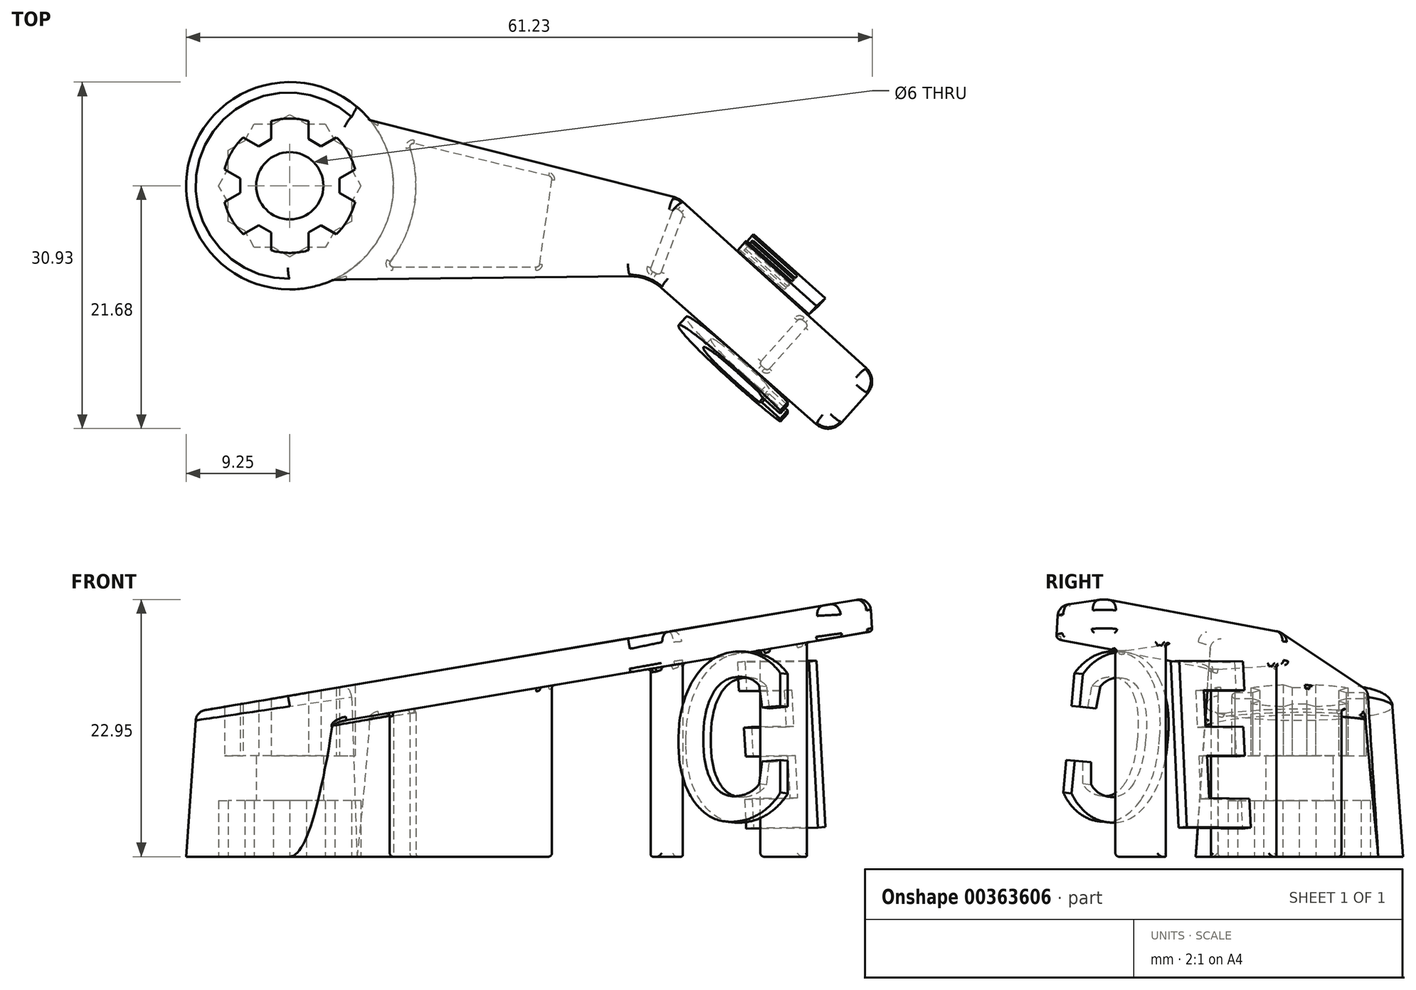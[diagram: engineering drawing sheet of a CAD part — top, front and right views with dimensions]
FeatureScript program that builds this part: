
annotation { "Feature Type Name" : "Feature", "Feature Type Description" : "" }
export const myFeature = defineFeature(function(context is Context, id is Id, definition is map)
    precondition{}
    {
        {
            var Q0;
            Q0=qCreatedBy(makeId("Top.planeOp"),FACE);
            var sketch = newSketch(context, id + "F0", { "sketchPlane" : qUnion([Q0])});
            skCircle(sketch, "E0", {"center": v(0, 0) * mm, "radius": 9.25 * mm});
            skCircle(sketch, "E1", {"center": v(0, 0) * mm, "radius": 3 * mm});
            skLineSegment(sketch, "E2", {"start": v(0, -9.25) * mm, "end": v(30.35, -9.25) * mm});
            skLineSegment(sketch, "E3", {"start": v(32.35, -10.02) * mm, "end": v(46.06, -22.3) * mm});
            skLineSegment(sketch, "E4", {"start": v(50.3, -22.07) * mm, "end": v(52.63, -19.46) * mm});
            skLineSegment(sketch, "E5", {"start": v(52.4, -15.22) * mm, "end": v(35.86, -0.5) * mm});
            skLineSegment(sketch, "E6", {"start": v(34.56, 0.18) * mm, "end": v(6, 7.05) * mm});
            skPoint(sketch, "E7.visualSharp", {"position": v(48.3, -24.3) * mm});
            skArc(sketch, "E7.filletArc", {"start": v(46.06, -22.3) * mm, "mid": v(48.23, -23.06) * mm, "end": v(50.3, -22.07) * mm});
            skPoint(sketch, "E8.visualSharp", {"position": v(54.64, -17.22) * mm});
            skArc(sketch, "E8.filletArc", {"start": v(52.63, -19.46) * mm, "mid": v(53.4, -17.3) * mm, "end": v(52.4, -15.22) * mm});
            skPoint(sketch, "E9.visualSharp", {"position": v(35.3, 0) * mm});
            skArc(sketch, "E9.filletArc", {"start": v(35.86, -0.5) * mm, "mid": v(35.25, -0.08) * mm, "end": v(34.56, 0.18) * mm});
            skPoint(sketch, "E10.visualSharp", {"position": v(31.5, -9.25) * mm});
            skArc(sketch, "E10.filletArc", {"start": v(32.35, -10.02) * mm, "mid": v(31.42, -9.45) * mm, "end": v(30.35, -9.25) * mm});
            skSolve(sketch);
        }
        {
            var Q0;
            Q0=makeQuery(id+"F0.imprint","IMPRINT",FACE,{"disambiguationData":[TD([[makeQuery(id+"F0.imprint","IMPRINT",EDGE,{"derivedFrom":sQuery(id+"F0.wireOp",EDGE,"E1")}),-1.0]])]});
            var Q1;
            Q1=makeQuery(id+"F0.imprint","IMPRINT",FACE,{"disambiguationData":[TD([[makeQuery(id+"F0.imprint","IMPRINT",EDGE,{"derivedFrom":sQuery(id+"F0.wireOp",EDGE,"E1")}),1.0]])]});
            var Q2;
            {var subQ0=sQuery(id+"F0.wireOp",EDGE,"E2");Q2=makeQuery(id+"F0.imprint","IMPRINT",FACE,{"disambiguationData":[TD([[makeQuery(id+"F0.imprint","IMPRINT",EDGE,{"derivedFrom":subQ0}),1.0]])]});}
            extrude(context, id + "F1", {"entities" : qUnion([Q0, Q1, Q2]), "depth" : 23 * mm, "hasDraft" : true, "draftAngle" : 4 * degree, "draftPullDirection" : true});
        }
        {
            var Q0;
            Q0=makeQuery(id+"F0.imprint","IMPRINT",FACE,{"disambiguationData":[TD([[makeQuery(id+"F0.imprint","IMPRINT",EDGE,{"derivedFrom":sQuery(id+"F0.wireOp",EDGE,"E1")}),1.0]])]});
            extrude(context, id + "F2", {"entities" : qUnion([Q0]), "operationType" : NewBodyOperationType.REMOVE, "endBound" : BoundingType.THROUGH_ALL, "depth" : 25 * mm});
        }
        {
            var Q0;
            Q0=makeQuery(id+"F1.opExtrude","CAP_FACE",FACE,{"disambiguationData":[OSD([sQuery(id+"F0.wireOp",EDGE,"E0"),sQuery(id+"F0.wireOp",EDGE,"E2"),sQuery(id+"F0.wireOp",EDGE,"E3"),sQuery(id+"F0.wireOp",EDGE,"E4"),sQuery(id+"F0.wireOp",EDGE,"E5"),sQuery(id+"F0.wireOp",EDGE,"E6"),sQuery(id+"F0.wireOp",EDGE,"E7.filletArc"),sQuery(id+"F0.wireOp",EDGE,"E8.filletArc"),sQuery(id+"F0.wireOp",EDGE,"E9.filletArc"),sQuery(id+"F0.wireOp",EDGE,"E10.filletArc")])],"isStart":false});
            var sketch = newSketch(context, id + "F3", { "sketchPlane" : qUnion([Q0])});
            skCircle(sketch, "E11", {"center": v(0, 0) * mm, "radius": 6 * mm});
            skSolve(sketch);
        }
        {
            var Q0;
            Q0 = qSketchRegion(id + "F3", true);
            extrude(context, id + "F4", {"entities" : qUnion([Q0]), "operationType" : NewBodyOperationType.REMOVE, "oppositeDirection" : true, "depth" : 4.5 * mm});
        }
        {
            var Q0;
            Q0=makeQuery(id+"F0.imprint","IMPRINT",FACE,{"disambiguationData":[TD([[makeQuery(id+"F0.imprint","IMPRINT",EDGE,{"derivedFrom":sQuery(id+"F0.wireOp",EDGE,"E1")}),-1.0]])]});
            var sketch = newSketch(context, id + "F5", { "sketchPlane" : qUnion([Q0])});
            skCircle(sketch, "E12.cCircle", {"center": v(0, 0) * mm, "radius": 5.5 * mm, "construction": true});
            skLineSegment(sketch, "E12.0", {"start": v(5.5, 3.18) * mm, "end": v(5.5, -3.18) * mm});
            skLineSegment(sketch, "E12.1", {"start": v(5.5, -3.18) * mm, "end": v(0, -6.35) * mm});
            skLineSegment(sketch, "E12.2", {"start": v(0, -6.35) * mm, "end": v(-5.5, -3.18) * mm});
            skLineSegment(sketch, "E12.3", {"start": v(-5.5, -3.18) * mm, "end": v(-5.5, 3.18) * mm});
            skLineSegment(sketch, "E12.4", {"start": v(-5.5, 3.18) * mm, "end": v(0, 6.35) * mm});
            skLineSegment(sketch, "E12.5", {"start": v(0, 6.35) * mm, "end": v(5.5, 3.18) * mm});
            skPoint(sketch, "E12.0.midPoint", {"position": v(5.5, 0) * mm});
            skLineSegment(sketch, "E13.0", {"start": v(6.35, 0) * mm, "end": v(3.18, -5.5) * mm});
            skLineSegment(sketch, "E13.1", {"start": v(3.18, -5.5) * mm, "end": v(-3.18, -5.5) * mm});
            skLineSegment(sketch, "E13.2", {"start": v(-3.18, -5.5) * mm, "end": v(-6.35, 0) * mm});
            skLineSegment(sketch, "E13.3", {"start": v(-6.35, 0) * mm, "end": v(-3.18, 5.5) * mm});
            skLineSegment(sketch, "E13.4", {"start": v(-3.18, 5.5) * mm, "end": v(3.18, 5.5) * mm});
            skLineSegment(sketch, "E13.5", {"start": v(3.18, 5.5) * mm, "end": v(6.35, 0) * mm});
            skPoint(sketch, "E13.0.midPoint", {"position": v(4.76, -2.75) * mm});
            skSolve(sketch);
        }
        {
            var Q0;
            Q0=makeQuery(id+"F5.imprint","IMPRINT",FACE,{"disambiguationData":[TD([[makeQuery(id+"F5.imprint","IMPRINT",EDGE,{"derivedFrom":makeQuery(id+"F0.imprint","IMPRINT",EDGE,{"derivedFrom":sQuery(id+"F0.wireOp",EDGE,"E1")})}),-1.0]])]});
            var Q1;
            {var subQ0=sQuery(id+"F5.wireOp",EDGE,"E12.4");var subQ1=sQuery(id+"F5.wireOp",EDGE,"E12.3");var subQ2=makeQuery(id+"F5.imprint","INTERSECT",VERTEX,{"derivedFrom":[subQ1,subQ0]});Q1=makeQuery(id+"F5.imprint","IMPRINT",FACE,{"disambiguationData":[TD([[makeQuery(id+"F5.imprint","IMPRINT",EDGE,{"disambiguationData":[TD([[subQ2,1.0]])],"derivedFrom":subQ1}),-1.0]])]});}
            var Q2;
            {var subQ0=sQuery(id+"F5.wireOp",EDGE,"E13.2");var subQ1=sQuery(id+"F5.wireOp",EDGE,"E12.3");var subQ2=makeQuery(id+"F5.imprint","INTERSECT",VERTEX,{"derivedFrom":[subQ1,subQ0]});Q2=makeQuery(id+"F5.imprint","IMPRINT",FACE,{"disambiguationData":[TD([[makeQuery(id+"F5.imprint","IMPRINT",EDGE,{"disambiguationData":[TD([[subQ2,-1.0]])],"derivedFrom":subQ1}),1.0]])]});}
            var Q3;
            {var subQ0=sQuery(id+"F5.wireOp",EDGE,"E12.3");var subQ1=sQuery(id+"F5.wireOp",EDGE,"E12.2");var subQ2=makeQuery(id+"F5.imprint","INTERSECT",VERTEX,{"derivedFrom":[subQ1,subQ0]});Q3=makeQuery(id+"F5.imprint","IMPRINT",FACE,{"disambiguationData":[TD([[makeQuery(id+"F5.imprint","IMPRINT",EDGE,{"disambiguationData":[TD([[subQ2,1.0]])],"derivedFrom":subQ1}),-1.0]])]});}
            var Q4;
            {var subQ0=sQuery(id+"F5.wireOp",EDGE,"E13.1");var subQ1=sQuery(id+"F5.wireOp",EDGE,"E12.2");var subQ2=makeQuery(id+"F5.imprint","INTERSECT",VERTEX,{"derivedFrom":[subQ1,subQ0]});Q4=makeQuery(id+"F5.imprint","IMPRINT",FACE,{"disambiguationData":[TD([[makeQuery(id+"F5.imprint","IMPRINT",EDGE,{"disambiguationData":[TD([[subQ2,-1.0]])],"derivedFrom":subQ1}),1.0]])]});}
            var Q5;
            {var subQ0=sQuery(id+"F5.wireOp",EDGE,"E13.3");var subQ1=sQuery(id+"F5.wireOp",EDGE,"E12.4");var subQ2=makeQuery(id+"F5.imprint","INTERSECT",VERTEX,{"derivedFrom":[subQ1,subQ0]});Q5=makeQuery(id+"F5.imprint","IMPRINT",FACE,{"disambiguationData":[TD([[makeQuery(id+"F5.imprint","IMPRINT",EDGE,{"disambiguationData":[TD([[subQ2,-1.0]])],"derivedFrom":subQ1}),1.0]])]});}
            var Q6;
            {var subQ0=sQuery(id+"F5.wireOp",EDGE,"E12.5");var subQ1=sQuery(id+"F5.wireOp",EDGE,"E12.4");var subQ2=makeQuery(id+"F5.imprint","INTERSECT",VERTEX,{"derivedFrom":[subQ1,subQ0]});Q6=makeQuery(id+"F5.imprint","IMPRINT",FACE,{"disambiguationData":[TD([[makeQuery(id+"F5.imprint","IMPRINT",EDGE,{"disambiguationData":[TD([[subQ2,1.0]])],"derivedFrom":subQ1}),-1.0]])]});}
            var Q7;
            {var subQ0=sQuery(id+"F5.wireOp",EDGE,"E13.4");var subQ1=sQuery(id+"F5.wireOp",EDGE,"E12.5");var subQ2=makeQuery(id+"F5.imprint","INTERSECT",VERTEX,{"derivedFrom":[subQ1,subQ0]});Q7=makeQuery(id+"F5.imprint","IMPRINT",FACE,{"disambiguationData":[TD([[makeQuery(id+"F5.imprint","IMPRINT",EDGE,{"disambiguationData":[TD([[subQ2,-1.0]])],"derivedFrom":subQ1}),1.0]])]});}
            var Q8;
            {var subQ0=sQuery(id+"F5.wireOp",EDGE,"E12.5");var subQ1=sQuery(id+"F5.wireOp",EDGE,"E12.0");var subQ2=makeQuery(id+"F5.imprint","INTERSECT",VERTEX,{"derivedFrom":[subQ1,subQ0]});Q8=makeQuery(id+"F5.imprint","IMPRINT",FACE,{"disambiguationData":[TD([[makeQuery(id+"F5.imprint","IMPRINT",EDGE,{"disambiguationData":[TD([[subQ2,-1.0]])],"derivedFrom":subQ1}),-1.0]])]});}
            var Q9;
            {var subQ0=sQuery(id+"F5.wireOp",EDGE,"E13.5");var subQ1=sQuery(id+"F5.wireOp",EDGE,"E12.0");var subQ2=makeQuery(id+"F5.imprint","INTERSECT",VERTEX,{"derivedFrom":[subQ1,subQ0]});Q9=makeQuery(id+"F5.imprint","IMPRINT",FACE,{"disambiguationData":[TD([[makeQuery(id+"F5.imprint","IMPRINT",EDGE,{"disambiguationData":[TD([[subQ2,-1.0]])],"derivedFrom":subQ1}),1.0]])]});}
            var Q10;
            {var subQ0=sQuery(id+"F5.wireOp",EDGE,"E12.1");var subQ1=sQuery(id+"F5.wireOp",EDGE,"E12.0");var subQ2=makeQuery(id+"F5.imprint","INTERSECT",VERTEX,{"derivedFrom":[subQ1,subQ0]});Q10=makeQuery(id+"F5.imprint","IMPRINT",FACE,{"disambiguationData":[TD([[makeQuery(id+"F5.imprint","IMPRINT",EDGE,{"disambiguationData":[TD([[subQ2,1.0]])],"derivedFrom":subQ1}),-1.0]])]});}
            var Q11;
            {var subQ0=sQuery(id+"F5.wireOp",EDGE,"E13.0");var subQ1=sQuery(id+"F5.wireOp",EDGE,"E12.1");var subQ2=makeQuery(id+"F5.imprint","INTERSECT",VERTEX,{"derivedFrom":[subQ1,subQ0]});Q11=makeQuery(id+"F5.imprint","IMPRINT",FACE,{"disambiguationData":[TD([[makeQuery(id+"F5.imprint","IMPRINT",EDGE,{"disambiguationData":[TD([[subQ2,-1.0]])],"derivedFrom":subQ1}),1.0]])]});}
            var Q12;
            {var subQ0=sQuery(id+"F5.wireOp",EDGE,"E12.2");var subQ1=sQuery(id+"F5.wireOp",EDGE,"E12.1");var subQ2=makeQuery(id+"F5.imprint","INTERSECT",VERTEX,{"derivedFrom":[subQ1,subQ0]});Q12=makeQuery(id+"F5.imprint","IMPRINT",FACE,{"disambiguationData":[TD([[makeQuery(id+"F5.imprint","IMPRINT",EDGE,{"disambiguationData":[TD([[subQ2,1.0]])],"derivedFrom":subQ1}),-1.0]])]});}
            extrude(context, id + "F6", {"entities" : qUnion([Q0, Q1, Q2, Q3, Q4, Q5, Q6, Q7, Q8, Q9, Q10, Q11, Q12]), "operationType" : NewBodyOperationType.REMOVE, "depth" : 5 * mm});
        }
        {
            var Q0;
            Q0=qCreatedBy(makeId("Front.planeOp"),FACE);
            var sketch = newSketch(context, id + "F7", { "sketchPlane" : qUnion([Q0])});
            skLineSegment(sketch, "E14", {"start": v(-7.94, 13.02) * mm, "end": v(51.08, 23) * mm});
            skLineSegment(sketch, "E15", {"start": v(-7.94, 13.02) * mm, "end": v(-7.94, 0.52) * mm});
            skLineSegment(sketch, "E16", {"start": v(51.08, 23) * mm, "end": v(51.08, 0) * mm});
            skSolve(sketch);
        }
        {
            var Q0;
            Q0=makeQuery(id+"F3.imprint","IMPRINT",FACE,{"disambiguationData":[TD([[makeQuery(id+"F3.imprint","IMPRINT",EDGE,{"derivedFrom":sQuery(id+"F3.wireOp",EDGE,"E11")}),1.0]])]});
            extrude(context, id + "F8", {"entities" : qUnion([Q0]), "operationType" : NewBodyOperationType.REMOVE, "oppositeDirection" : true, "depth" : 14 * mm});
        }
        {
            var Q0;
            Q0=sQuery(id+"F7.wireOp",EDGE,"E14");
            cPlane(context, id + "F9", {"entities" : qUnion([Q0]), "cplaneType" : CPlaneType.LINE_ANGLE, "offset" : 25 * mm, "angle" : 90 * degree, "width" : 150 * mm, "height" : 150 * mm});
        }
        {
            var Q0;
            Q0=qCreatedBy(id+"F9.planeOp",FACE);
            var sketch = newSketch(context, id + "F10", { "sketchPlane" : qUnion([Q0])});
            skLineSegment(sketch, "E17.bottom", {"start": v(59.4, 33.58) * mm, "end": v(-10.14, 33.58) * mm});
            skLineSegment(sketch, "E17.top", {"start": v(59.4, -33.19) * mm, "end": v(-10.14, -33.19) * mm});
            skLineSegment(sketch, "E17.left", {"start": v(59.4, 33.58) * mm, "end": v(59.4, -33.19) * mm});
            skLineSegment(sketch, "E17.right", {"start": v(-10.14, 33.58) * mm, "end": v(-10.14, -33.19) * mm});
            skSolve(sketch);
        }
        {
            var Q0;
            Q0=makeQuery(id+"F8.boolean.opBoolean","COPY",FACE,{"derivedFrom":makeQuery(id+"F8.opExtrude","CAP_FACE",FACE,{"disambiguationData":[OSD([sQuery(id+"F0.wireOp",EDGE,"E0"),sQuery(id+"F0.wireOp",EDGE,"E1"),sQuery(id+"F0.wireOp",EDGE,"E2"),sQuery(id+"F0.wireOp",EDGE,"E3"),sQuery(id+"F0.wireOp",EDGE,"E4"),sQuery(id+"F0.wireOp",EDGE,"E5"),sQuery(id+"F0.wireOp",EDGE,"E6"),sQuery(id+"F0.wireOp",EDGE,"E7.filletArc"),sQuery(id+"F0.wireOp",EDGE,"E8.filletArc"),sQuery(id+"F0.wireOp",EDGE,"E9.filletArc"),sQuery(id+"F0.wireOp",EDGE,"E10.filletArc"),sQuery(id+"F3.wireOp",EDGE,"E11")])],"isStart":false})});
            var sketch = newSketch(context, id + "F11", { "sketchPlane" : qUnion([Q0])});
            skLineSegment(sketch, "E18", {"start": v(1.66, -5.77) * mm, "end": v(1.66, -4.17) * mm});
            skLineSegment(sketch, "E19", {"start": v(1.66, -4.17) * mm, "end": v(2.78, -3.52) * mm});
            skLineSegment(sketch, "E20", {"start": v(2.78, -3.52) * mm, "end": v(4.16, -4.32) * mm});
            skLineSegment(sketch, "E21.1.0", {"start": v(4.44, -0.64) * mm, "end": v(4.44, 0.64) * mm});
            skLineSegment(sketch, "E21.1.1", {"start": v(4.44, 0.64) * mm, "end": v(5.82, 1.44) * mm});
            skLineSegment(sketch, "E21.1.2", {"start": v(5.82, -1.44) * mm, "end": v(4.44, -0.64) * mm});
            skLineSegment(sketch, "E21.2.0", {"start": v(2.78, 3.52) * mm, "end": v(1.66, 4.17) * mm});
            skLineSegment(sketch, "E21.2.1", {"start": v(1.66, 4.17) * mm, "end": v(1.66, 5.77) * mm});
            skLineSegment(sketch, "E21.2.2", {"start": v(4.16, 4.32) * mm, "end": v(2.78, 3.52) * mm});
            skLineSegment(sketch, "E21.3.0", {"start": v(-1.66, 4.17) * mm, "end": v(-2.78, 3.52) * mm});
            skLineSegment(sketch, "E21.3.1", {"start": v(-2.78, 3.52) * mm, "end": v(-4.16, 4.32) * mm});
            skLineSegment(sketch, "E21.3.2", {"start": v(-1.66, 5.77) * mm, "end": v(-1.66, 4.17) * mm});
            skLineSegment(sketch, "E21.4.0", {"start": v(-4.44, 0.64) * mm, "end": v(-4.44, -0.64) * mm});
            skLineSegment(sketch, "E21.4.1", {"start": v(-4.44, -0.64) * mm, "end": v(-5.82, -1.44) * mm});
            skLineSegment(sketch, "E21.4.2", {"start": v(-5.82, 1.44) * mm, "end": v(-4.44, 0.64) * mm});
            skLineSegment(sketch, "E21.5.0", {"start": v(-2.78, -3.52) * mm, "end": v(-1.66, -4.17) * mm});
            skLineSegment(sketch, "E21.5.1", {"start": v(-1.66, -4.17) * mm, "end": v(-1.66, -5.77) * mm});
            skLineSegment(sketch, "E21.5.2", {"start": v(-4.16, -4.32) * mm, "end": v(-2.78, -3.52) * mm});
            skPoint(sketch, "E21.center", {"position": v(0, 0) * mm});
            skSolve(sketch);
        }
        {
            var Q0;
            Q0=makeQuery(id+"F11.imprint","IMPRINT",FACE,{"disambiguationData":[TD([[makeQuery(id+"F11.imprint","IMPRINT",EDGE,{"derivedFrom":sQuery(id+"F11.wireOp",EDGE,"E21.5.0")}),-1.0]])]});
            var Q1;
            Q1=makeQuery(id+"F11.imprint","IMPRINT",FACE,{"disambiguationData":[TD([[makeQuery(id+"F11.imprint","IMPRINT",EDGE,{"derivedFrom":sQuery(id+"F11.wireOp",EDGE,"E21.4.0")}),-1.0]])]});
            var Q2;
            Q2=makeQuery(id+"F11.imprint","IMPRINT",FACE,{"disambiguationData":[TD([[makeQuery(id+"F11.imprint","IMPRINT",EDGE,{"derivedFrom":sQuery(id+"F11.wireOp",EDGE,"E21.3.0")}),-1.0]])]});
            var Q3;
            Q3=makeQuery(id+"F11.imprint","IMPRINT",FACE,{"disambiguationData":[TD([[makeQuery(id+"F11.imprint","IMPRINT",EDGE,{"derivedFrom":sQuery(id+"F11.wireOp",EDGE,"E21.2.0")}),-1.0]])]});
            var Q4;
            Q4=makeQuery(id+"F11.imprint","IMPRINT",FACE,{"disambiguationData":[TD([[makeQuery(id+"F11.imprint","IMPRINT",EDGE,{"derivedFrom":sQuery(id+"F11.wireOp",EDGE,"E21.1.0")}),-1.0]])]});
            var Q5;
            {var subQ0=sQuery(id+"F11.wireOp",EDGE,"E18");Q5=makeQuery(id+"F11.imprint","IMPRINT",FACE,{"disambiguationData":[TD([[makeQuery(id+"F11.imprint","IMPRINT",EDGE,{"derivedFrom":subQ0}),-1.0]])]});}
            extrude(context, id + "F12", {"entities" : qUnion([Q0, Q1, Q2, Q3, Q4, Q5]), "operationType" : NewBodyOperationType.ADD, "depth" : 10 * mm});
        }
        {
            var Q0;
            Q0 = qSketchRegion(id + "F10", true);
            extrude(context, id + "F13", {"entities" : qUnion([Q0]), "operationType" : NewBodyOperationType.REMOVE, "depth" : 25 * mm});
        }
        {
            var Q0;
            Q0=makeQuery(id+"F1.opExtrude","SWEPT_EDGE",EDGE,{"disambiguationData":[OSD([sQuery(id+"F0.wireOp",EDGE,"E4"),sQuery(id+"F0.wireOp",EDGE,"E7.filletArc")])]});
            var Q1;
            Q1=makeQuery(id+"F13.boolean.opBoolean","INTERSECT",EDGE,{"derivedFrom":[makeQuery(id+"F1.opExtrude","SWEPT_FACE",FACE,{"disambiguationData":[OSD([sQuery(id+"F0.wireOp",EDGE,"E3")])]}),makeQuery(id+"F13.opExtrude","CAP_FACE",FACE,{"disambiguationData":[OSD([sQuery(id+"F10.wireOp",EDGE,"E17.bottom"),sQuery(id+"F10.wireOp",EDGE,"E17.top"),sQuery(id+"F10.wireOp",EDGE,"E17.left"),sQuery(id+"F10.wireOp",EDGE,"E17.right")])],"isStart":true})]});
            var Q2;
            Q2=makeQuery(id+"F13.boolean.opBoolean","INTERSECT",EDGE,{"derivedFrom":[makeQuery(id+"F1.opExtrude","SWEPT_FACE",FACE,{"disambiguationData":[OSD([sQuery(id+"F0.wireOp",EDGE,"E5")])]}),makeQuery(id+"F13.opExtrude","CAP_FACE",FACE,{"disambiguationData":[OSD([sQuery(id+"F10.wireOp",EDGE,"E17.bottom"),sQuery(id+"F10.wireOp",EDGE,"E17.top"),sQuery(id+"F10.wireOp",EDGE,"E17.left"),sQuery(id+"F10.wireOp",EDGE,"E17.right")])],"isStart":true})]});
            fillet(context, id + "F14", {"entities" : qUnion([Q0, Q1, Q2]), "radius" : 1 * mm, "tangentPropagation" : true, "allowEdgeOverflow" : false});
        }
        {
            var Q0;
            {var subQ0=sQuery(id+"F0.wireOp",EDGE,"E2");Q0=makeQuery(id+"F0.imprint","IMPRINT",FACE,{"disambiguationData":[TD([[makeQuery(id+"F0.imprint","IMPRINT",EDGE,{"derivedFrom":subQ0}),1.0]])]});}
            var sketch = newSketch(context, id + "F15", { "sketchPlane" : qUnion([Q0])});
            skLineSegment(sketch, "E22.0.0", {"start": v(50.3, -22.07) * mm, "end": v(52.63, -19.46) * mm});
            skArc(sketch, "E22.0.1", {"start": v(52.63, -19.46) * mm, "mid": v(53.4, -17.3) * mm, "end": v(52.4, -15.22) * mm});
            skLineSegment(sketch, "E22.0.2", {"start": v(52.4, -15.22) * mm, "end": v(35.86, -0.5) * mm});
            skArc(sketch, "E22.0.3", {"start": v(35.86, -0.5) * mm, "mid": v(35.25, -0.08) * mm, "end": v(34.56, 0.18) * mm});
            skLineSegment(sketch, "E22.0.4", {"start": v(34.56, 0.18) * mm, "end": v(6, 7.05) * mm});
            skArc(sketch, "E22.0.5", {"start": v(6, 7.05) * mm, "mid": v(8.68, -3.2) * mm, "end": v(0, -9.25) * mm});
            skLineSegment(sketch, "E22.0.6", {"start": v(0, -9.25) * mm, "end": v(30.35, -9.25) * mm});
            skArc(sketch, "E22.0.7", {"start": v(30.35, -9.25) * mm, "mid": v(31.42, -9.45) * mm, "end": v(32.35, -10.02) * mm});
            skLineSegment(sketch, "E22.0.8", {"start": v(32.35, -10.02) * mm, "end": v(46.06, -22.3) * mm});
            skArc(sketch, "E22.0.9", {"start": v(46.06, -22.3) * mm, "mid": v(48.23, -23.06) * mm, "end": v(50.3, -22.07) * mm});
            skArc(sketch, "E23.0", {"start": v(10.56, 3.9) * mm, "mid": v(11.08, -1.94) * mm, "end": v(8.6, -7.25) * mm});
            skLineSegment(sketch, "E23.1", {"start": v(34.34, -1.83) * mm, "end": v(10.56, 3.9) * mm});
            skArc(sketch, "E23.2", {"start": v(30.35, -7.25) * mm, "mid": v(32.14, -7.58) * mm, "end": v(33.69, -8.53) * mm});
            skLineSegment(sketch, "E23.3", {"start": v(33.69, -8.53) * mm, "end": v(48.14, -21.48) * mm});
            skLineSegment(sketch, "E23.4", {"start": v(48.14, -21.48) * mm, "end": v(51.81, -17.38) * mm});
            skLineSegment(sketch, "E23.5", {"start": v(8.6, -7.25) * mm, "end": v(30.35, -7.25) * mm});
            skLineSegment(sketch, "E23.6", {"start": v(51.81, -17.38) * mm, "end": v(34.34, -1.83) * mm});
            skLineSegment(sketch, "E24", {"start": v(21.26, -7.25) * mm, "end": v(22.45, 1.03) * mm});
            skLineSegment(sketch, "E25", {"start": v(32.14, -7.58) * mm, "end": v(34.34, -1.83) * mm});
            skLineSegment(sketch, "E26", {"start": v(41.88, -15.87) * mm, "end": v(45.52, -11.78) * mm});
            skLineSegment(sketch, "E27.0", {"start": v(22.27, -7.25) * mm, "end": v(23.42, 0.8) * mm});
            skLineSegment(sketch, "E28.0", {"start": v(33.04, -8.03) * mm, "end": v(35.14, -2.54) * mm});
            skLineSegment(sketch, "E29.0", {"start": v(42.63, -16.54) * mm, "end": v(46.27, -12.45) * mm});
            skSolve(sketch);
        }
        {
            var Q0;
            Q0=makeQuery(id+"F13.boolean.opBoolean","COPY",FACE,{"derivedFrom":makeQuery(id+"F13.opExtrude","CAP_FACE",FACE,{"disambiguationData":[OSD([sQuery(id+"F10.wireOp",EDGE,"E17.bottom"),sQuery(id+"F10.wireOp",EDGE,"E17.top"),sQuery(id+"F10.wireOp",EDGE,"E17.left"),sQuery(id+"F10.wireOp",EDGE,"E17.right")])],"isStart":true})});
            cPlane(context, id + "F16", {"entities" : qUnion([Q0]), "cplaneType" : CPlaneType.OFFSET, "offset" : 3 * mm, "oppositeDirection" : true, "width" : 150 * mm, "height" : 150 * mm});
        }
        {
            var Q0;
            {var subQ0=sQuery(id+"F15.wireOp",EDGE,"E23.4");Q0=makeQuery(id+"F15.imprint","IMPRINT",FACE,{"disambiguationData":[TD([[makeQuery(id+"F15.imprint","IMPRINT",EDGE,{"derivedFrom":subQ0}),1.0]])]});}
            var Q1;
            {var subQ0=sQuery(id+"F15.wireOp",EDGE,"E26");Q1=makeQuery(id+"F15.imprint","IMPRINT",FACE,{"disambiguationData":[TD([[makeQuery(id+"F15.imprint","IMPRINT",EDGE,{"derivedFrom":subQ0}),1.0]])]});}
            var Q2;
            {var subQ4=sQuery(id+"F15.wireOp",EDGE,"E25");Q2=makeQuery(id+"F15.imprint","IMPRINT",FACE,{"disambiguationData":[TD([[makeQuery(id+"F15.imprint","IMPRINT",EDGE,{"derivedFrom":subQ4}),1.0]])]});}
            var Q3;
            {var subQ0=sQuery(id+"F15.wireOp",EDGE,"E23.0");Q3=makeQuery(id+"F15.imprint","IMPRINT",FACE,{"disambiguationData":[TD([[makeQuery(id+"F15.imprint","IMPRINT",EDGE,{"derivedFrom":subQ0}),1.0]])]});}
            var Q4;
            Q4=qCreatedBy(id+"F16.planeOp",FACE);
            extrude(context, id + "F17", {"entities" : qUnion([Q0, Q1, Q2, Q3]), "operationType" : NewBodyOperationType.REMOVE, "endBound" : BoundingType.UP_TO_SURFACE, "endBoundEntityFace" : qUnion([Q4]), "depth" : 25 * mm});
        }
        {
            var Q0;
            {var subQ0=sQuery(id+"F15.wireOp",EDGE,"E23.6");var subQ1=sQuery(id+"F15.wireOp",EDGE,"E23.3");var subQ2=sQuery(id+"F15.wireOp",EDGE,"E23.5");var subQ3=sQuery(id+"F15.wireOp",EDGE,"E23.2");var subQ4=sQuery(id+"F15.wireOp",EDGE,"E23.1");Q0=qUnion([makeQuery(id+"F17.boolean.opBoolean","COPY",FACE,{"derivedFrom":makeQuery(id+"F17.opExtrude","CAP_FACE",FACE,{"disambiguationData":[OSD([subQ3,subQ1,subQ0,sQuery(id+"F15.wireOp",EDGE,"E26"),sQuery(id+"F15.wireOp",EDGE,"E28.0")])],"isStart":false})}),makeQuery(id+"F17.boolean.opBoolean","COPY",FACE,{"derivedFrom":makeQuery(id+"F17.opExtrude","CAP_FACE",FACE,{"disambiguationData":[OSD([sQuery(id+"F15.wireOp",EDGE,"E23.0"),subQ4,subQ2,sQuery(id+"F15.wireOp",EDGE,"E24")])],"isStart":false})}),makeQuery(id+"F17.boolean.opBoolean","COPY",FACE,{"derivedFrom":makeQuery(id+"F17.opExtrude","CAP_FACE",FACE,{"disambiguationData":[OSD([subQ4,subQ3,subQ2,sQuery(id+"F15.wireOp",EDGE,"E25"),sQuery(id+"F15.wireOp",EDGE,"E27.0")])],"isStart":false})}),makeQuery(id+"F17.boolean.opBoolean","COPY",FACE,{"derivedFrom":makeQuery(id+"F17.opExtrude","CAP_FACE",FACE,{"disambiguationData":[OSD([subQ1,sQuery(id+"F15.wireOp",EDGE,"E23.4"),subQ0,sQuery(id+"F15.wireOp",EDGE,"E29.0")])],"isStart":false})})]);}
            var Q1;
            Q1=makeQuery(id+"F17.boolean.opBoolean","COPY",EDGE,{"derivedFrom":makeQuery(id+"F17.opExtrude","SWEPT_EDGE",EDGE,{"disambiguationData":[OSD([sQuery(id+"F15.wireOp",EDGE,"E23.1"),sQuery(id+"F15.wireOp",EDGE,"E24")])]})});
            var Q2;
            Q2=makeQuery(id+"F17.boolean.opBoolean","COPY",EDGE,{"derivedFrom":makeQuery(id+"F17.opExtrude","SWEPT_EDGE",EDGE,{"disambiguationData":[OSD([sQuery(id+"F15.wireOp",EDGE,"E23.5"),sQuery(id+"F15.wireOp",EDGE,"E24")])]})});
            var Q3;
            Q3=makeQuery(id+"F17.boolean.opBoolean","COPY",FACE,{"derivedFrom":makeQuery(id+"F17.opExtrude","SWEPT_FACE",FACE,{"disambiguationData":[OSD([sQuery(id+"F15.wireOp",EDGE,"E23.0")])]})});
            var Q4;
            {var subQ0=sQuery(id+"F15.wireOp",EDGE,"E23.1");Q4=makeQuery(id+"F17.boolean.opBoolean","COPY",FACE,{"derivedFrom":makeQuery(id+"F17.opExtrude","SWEPT_FACE",FACE,{"disambiguationData":[OSD([subQ0]),TDD([makeQuery(id+"F15.imprint","IMPRINT",EDGE,{"disambiguationData":[TD([[makeQuery(id+"F15.imprint","INTERSECT",VERTEX,{"derivedFrom":[subQ0,sQuery(id+"F15.wireOp",EDGE,"E27.0")]}),1.0]])],"derivedFrom":subQ0})])]})});}
            var Q5;
            {var subQ0=sQuery(id+"F15.wireOp",EDGE,"E23.5");Q5=makeQuery(id+"F17.boolean.opBoolean","COPY",FACE,{"derivedFrom":makeQuery(id+"F17.opExtrude","SWEPT_FACE",FACE,{"disambiguationData":[OSD([subQ0]),TDD([makeQuery(id+"F15.imprint","IMPRINT",EDGE,{"disambiguationData":[TD([[makeQuery(id+"F15.imprint","INTERSECT",VERTEX,{"derivedFrom":[sQuery(id+"F15.wireOp",EDGE,"E23.2"),subQ0]}),1.0]])],"derivedFrom":subQ0})])]})});}
            var Q6;
            {var subQ0=sQuery(id+"F15.wireOp",EDGE,"E23.3");Q6=makeQuery(id+"F17.boolean.opBoolean","COPY",FACE,{"derivedFrom":makeQuery(id+"F17.opExtrude","SWEPT_FACE",FACE,{"disambiguationData":[OSD([subQ0]),TDD([makeQuery(id+"F15.imprint","IMPRINT",EDGE,{"disambiguationData":[TD([[makeQuery(id+"F15.imprint","INTERSECT",VERTEX,{"derivedFrom":[sQuery(id+"F15.wireOp",EDGE,"E23.2"),subQ0]}),-1.0]])],"derivedFrom":subQ0})])]})});}
            var Q7;
            {var subQ0=sQuery(id+"F15.wireOp",EDGE,"E23.6");Q7=makeQuery(id+"F17.boolean.opBoolean","COPY",FACE,{"derivedFrom":makeQuery(id+"F17.opExtrude","SWEPT_FACE",FACE,{"disambiguationData":[OSD([subQ0]),TDD([makeQuery(id+"F15.imprint","IMPRINT",EDGE,{"disambiguationData":[TD([[makeQuery(id+"F15.imprint","INTERSECT",VERTEX,{"derivedFrom":[subQ0,sQuery(id+"F15.wireOp",EDGE,"E26")]}),-1.0]])],"derivedFrom":subQ0})])]})});}
            var Q8;
            Q8=makeQuery(id+"F17.boolean.opBoolean","COPY",FACE,{"derivedFrom":makeQuery(id+"F17.opExtrude","SWEPT_FACE",FACE,{"disambiguationData":[OSD([sQuery(id+"F15.wireOp",EDGE,"E23.4")])]})});
            var Q9;
            Q9=makeQuery(id+"F17.boolean.opBoolean","COPY",FACE,{"derivedFrom":makeQuery(id+"F17.opExtrude","SWEPT_FACE",FACE,{"disambiguationData":[OSD([sQuery(id+"F15.wireOp",EDGE,"E29.0")])]})});
            var Q10;
            {var subQ0=sQuery(id+"F15.wireOp",EDGE,"E23.6");Q10=makeQuery(id+"F17.boolean.opBoolean","COPY",FACE,{"derivedFrom":makeQuery(id+"F17.opExtrude","SWEPT_FACE",FACE,{"disambiguationData":[OSD([subQ0]),TDD([makeQuery(id+"F15.imprint","IMPRINT",EDGE,{"disambiguationData":[TD([[makeQuery(id+"F15.imprint","INTERSECT",VERTEX,{"derivedFrom":[sQuery(id+"F15.wireOp",EDGE,"E23.4"),subQ0]}),-1.0]])],"derivedFrom":subQ0})])]})});}
            var Q11;
            Q11=makeQuery(id+"F17.boolean.opBoolean","COPY",FACE,{"derivedFrom":makeQuery(id+"F17.opExtrude","SWEPT_FACE",FACE,{"disambiguationData":[OSD([sQuery(id+"F15.wireOp",EDGE,"E26")])]})});
            var Q12;
            Q12=makeQuery(id+"F17.boolean.opBoolean","COPY",FACE,{"derivedFrom":makeQuery(id+"F17.opExtrude","SWEPT_FACE",FACE,{"disambiguationData":[OSD([sQuery(id+"F15.wireOp",EDGE,"E27.0")])]})});
            var Q13;
            Q13=makeQuery(id+"F17.boolean.opBoolean","COPY",FACE,{"derivedFrom":makeQuery(id+"F17.opExtrude","SWEPT_FACE",FACE,{"disambiguationData":[OSD([sQuery(id+"F15.wireOp",EDGE,"E25")])]})});
            var Q14;
            Q14=makeQuery(id+"F17.boolean.opBoolean","COPY",FACE,{"derivedFrom":makeQuery(id+"F17.opExtrude","SWEPT_FACE",FACE,{"disambiguationData":[OSD([sQuery(id+"F15.wireOp",EDGE,"E28.0")])]})});
            var Q15;
            {var subQ0=sQuery(id+"F15.wireOp",EDGE,"E23.3");Q15=makeQuery(id+"F17.boolean.opBoolean","COPY",FACE,{"derivedFrom":makeQuery(id+"F17.opExtrude","SWEPT_FACE",FACE,{"disambiguationData":[OSD([subQ0]),TDD([makeQuery(id+"F15.imprint","IMPRINT",EDGE,{"disambiguationData":[TD([[makeQuery(id+"F15.imprint","INTERSECT",VERTEX,{"derivedFrom":[subQ0,sQuery(id+"F15.wireOp",EDGE,"E23.4")]}),1.0]])],"derivedFrom":subQ0})])]})});}
            fillet(context, id + "F18", {"entities" : qUnion([Q0, Q1, Q2, Q3, Q4, Q5, Q6, Q7, Q8, Q9, Q10, Q11, Q12, Q13, Q14, Q15]), "radius" : .3 * mm, "tangentPropagation" : true, "allowEdgeOverflow" : false});
        }
        {
            var Q0;
            Q0=makeQuery(id+"F1.opExtrude","SWEPT_FACE",FACE,{"disambiguationData":[OSD([sQuery(id+"F0.wireOp",EDGE,"E3")])]});
            var sketch = newSketch(context, id + "F19", { "sketchPlane" : qUnion([Q0])});
            skText(sketch, "E30", { "text": "C", "fontName": "RobotoSlab-Bold.ttf"});
            const initialGuessF19  = {"E30": [0.03429, 0.00167, 1, 0, 0.015]};
            skSetInitialGuess(sketch, initialGuessF19);
            skSolve(sketch);
        }
        {
            var Q0;
            Q0 = qSketchRegion(id + "F19", true);
            extrude(context, id + "F20", {"entities" : qUnion([Q0]), "operationType" : NewBodyOperationType.ADD, "depth" : 1 * mm});
        }
        {
            var Q0;
            Q0=makeQuery(id+"F1.opExtrude","SWEPT_FACE",FACE,{"disambiguationData":[OSD([sQuery(id+"F0.wireOp",EDGE,"E5")])]});
            var sketch = newSketch(context, id + "F21", { "sketchPlane" : qUnion([Q0])});
            skText(sketch, "E31", { "text": "E", "fontName": "OpenSans-Bold.ttf"});
            const initialGuessF21  = {"E31": [-0.0441, 0.0037, 0.99756, -0.06976, 0.015]};
            skSetInitialGuess(sketch, initialGuessF21);
            skSolve(sketch);
        }
        {
            var Q0;
            Q0 = qSketchRegion(id + "F21", true);
            extrude(context, id + "F22", {"entities" : qUnion([Q0]), "operationType" : NewBodyOperationType.ADD, "depth" : 1 * mm});
        }
    });
